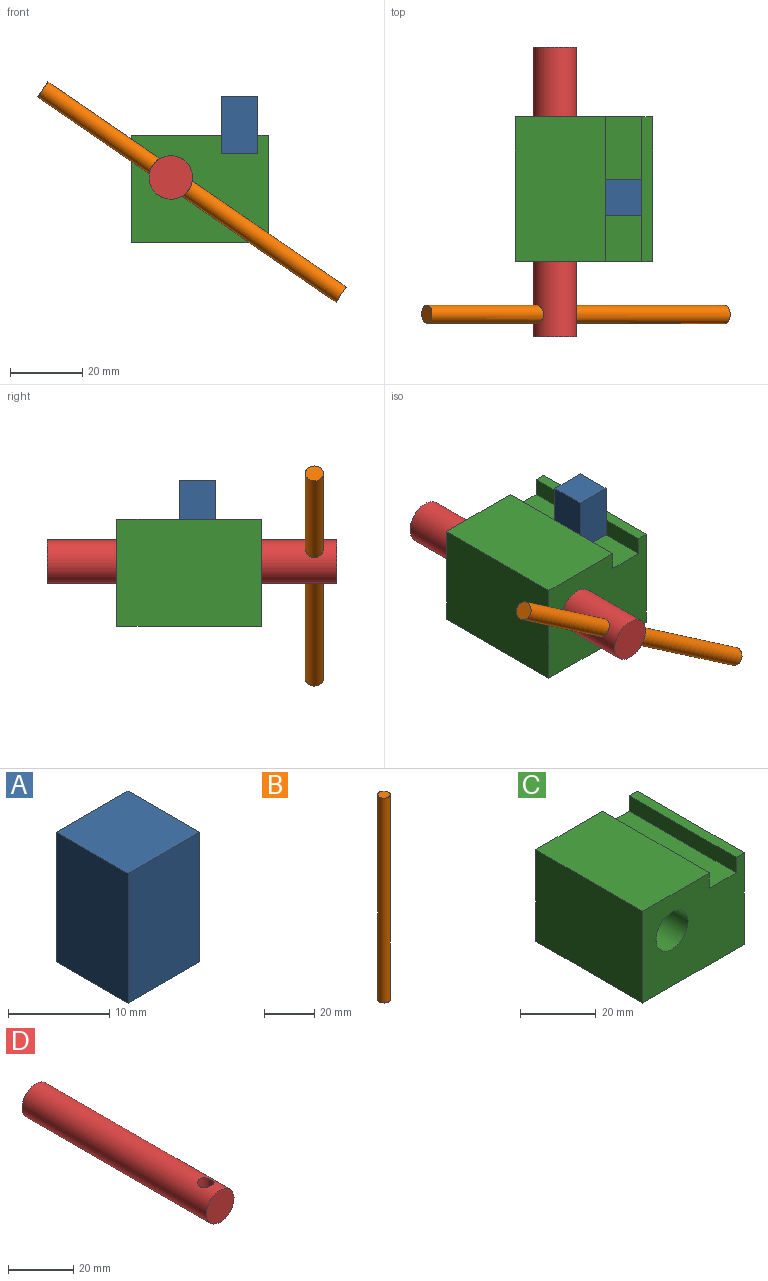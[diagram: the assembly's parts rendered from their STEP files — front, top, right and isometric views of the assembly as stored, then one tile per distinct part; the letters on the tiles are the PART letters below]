
ASSEMBLY  parts=4 mates=4
PART A: 6 faces, bbox 10x10x15.7 mm
  f0: plane 10x10mm, normal (0,0,1), area 100mm2, adj f1,f3,f4,f5
  f1: plane 15.7x10mm, normal (-1,0,0), area 157mm2, adj f0,f2,f4,f5
  f2: plane 10x10mm, normal (0,0,-1), area 100mm2, adj f1,f3,f4,f5
  f3: plane 15.7x10mm, normal (1,0,0), area 157mm2, adj f0,f2,f4,f5
  f4: plane 15.7x10mm, normal (0,-1,0), area 157mm2, adj f0,f1,f2,f3
  f5: plane 15.7x10mm, normal (0,1,0), area 157mm2, adj f0,f1,f2,f3
PART B: 3 faces, bbox 5x5x100 mm
  f0: cylinder r=2.5mm len=100mm, axis (0,0,-1), area 1570.8mm2, adj f1,f2
  f1: plane 5x5mm, normal (0,0,1), area 19.6mm2, adj f0
  f2: plane 5x5mm, normal (0,0,-1), area 19.6mm2, adj f0
PART C: 11 faces, bbox 38x40x29.7 mm
  f0: plane 40x3.03mm, normal (0,0,1), area 121.1mm2, adj f1,f7,f9,f10
  f1: plane 40x5mm, normal (-1,0,0), area 200mm2, adj f0,f2,f9,f10
  f2: plane 40x10mm, normal (0,0,1), area 400mm2, adj f1,f3,f9,f10
  f3: plane 40x5mm, normal (1,0,0), area 200mm2, adj f2,f4,f9,f10
  f4: plane 40x24.98mm, normal (0,0,1), area 999mm2, adj f3,f5,f9,f10
  f5: plane 40x29.67mm, normal (-1,0,0), area 1186.9mm2, adj f4,f6,f9,f10
  f6: plane 40x38mm, normal (0,0,-1), area 1520.1mm2, adj f5,f7,f9,f10
  f7: plane 40x29.67mm, normal (1,0,0), area 1186.9mm2, adj f0,f6,f9,f10
  f8: cylinder r=6mm len=40mm, axis (0,1,0), area 1508mm2, adj f9,f10
  f9: plane 38x29.67mm, normal (0,-1,0), area 964.5mm2, adj f0,f1,f2,f3,f4,f5,f6,f7
  f10: plane 38x29.67mm, normal (0,1,0), area 964.5mm2, adj f0,f1,f2,f3,f4,f5,f6,f7
PART D: 4 faces, bbox 12x80x12 mm
  f0: cylinder r=6mm len=80mm, axis (0,1,0), area 2975.7mm2, adj f1,f2,f3
  f1: plane 12x12mm, normal (0,-1,0), area 113.1mm2, adj f0
  f2: plane 12x12mm, normal (0,1,0), area 113.1mm2, adj f0
  f3: cylinder r=2.5mm len=12mm, axis (0,0,-1), area 180mm2, adj f0
PLACE A t=(19.44,7.08,111.89)mm
PLACE B rot(axis=(0,-1,0),55.5deg) t=(47.2,3.67,-33.5)mm
PLACE C t=(75.32,4.42,12.43)mm fixed
PLACE D rot(axis=(0,-1,0),55.5deg) t=(35.8,3.67,-13.52)mm
MATE cylindrical D.f0 <-> C.f8  axis (0,1,0) through (28.04,3.67,39.41)mm
MATE slider B.f0 <-> D.f3  axis (0.82,0,-0.57) through (33.9,-30.12,35.38)mm
MATE planar C.f1 <-> A.f3  axis (-1,0,0) through (52.04,4.42,48.61)mm
MATE planar C.f2 <-> A.f2  axis (0,0,1) through (47.04,4.42,46.11)mm
